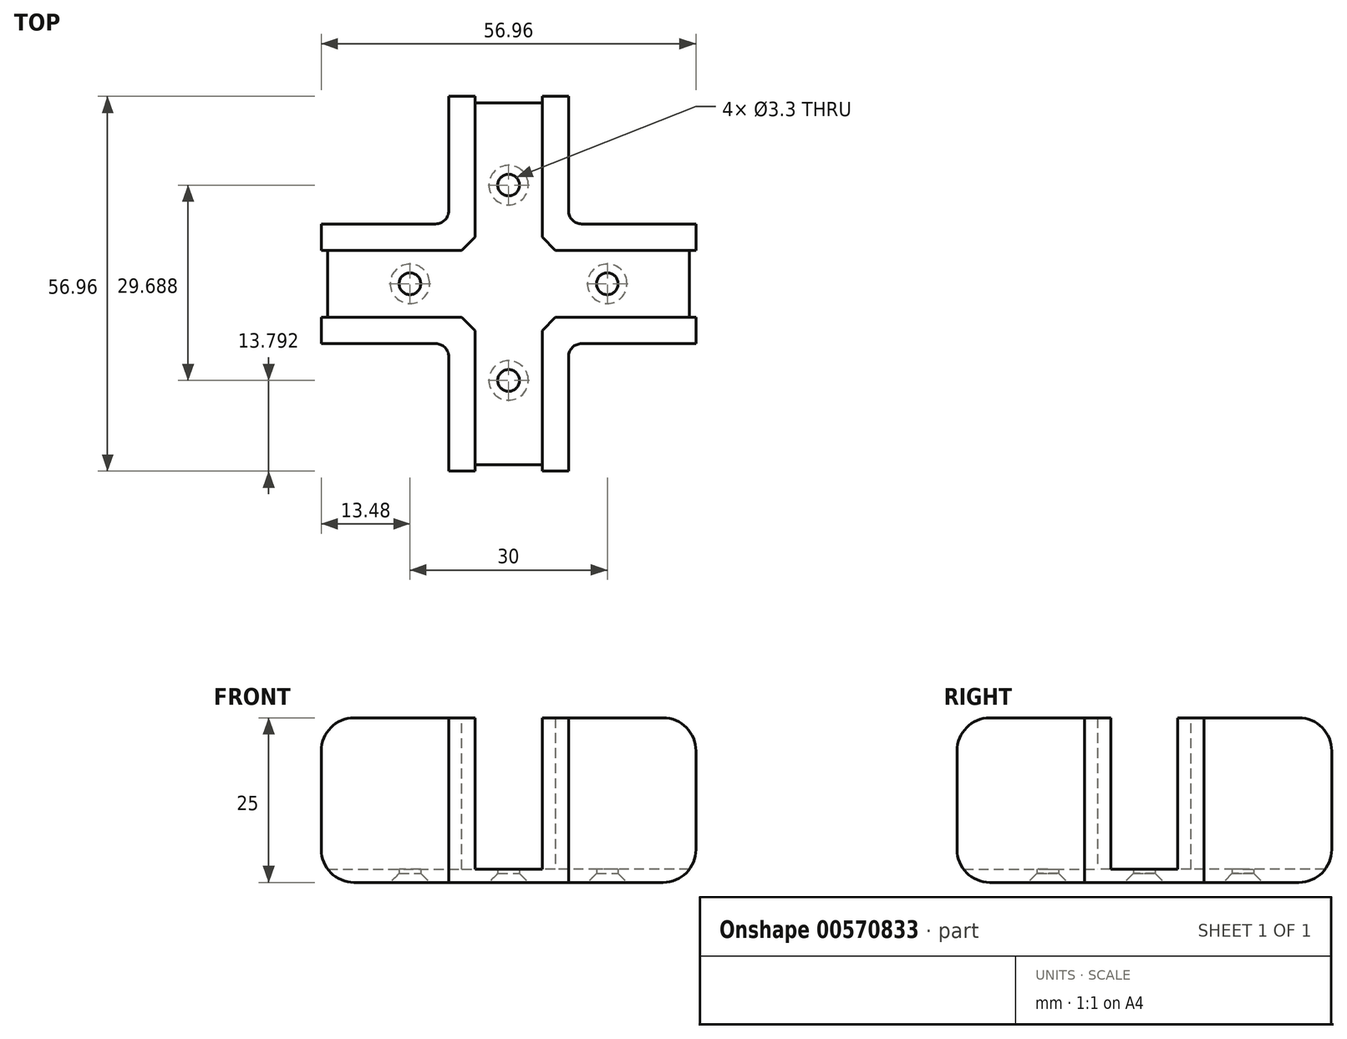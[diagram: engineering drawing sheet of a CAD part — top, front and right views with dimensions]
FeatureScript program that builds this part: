
annotation { "Feature Type Name" : "Feature", "Feature Type Description" : "" }
export const myFeature = defineFeature(function(context is Context, id is Id, definition is map)
    precondition{}
    {
        {
            var Q0;
            Q0=qCreatedBy(makeId("Top.planeOp"),FACE);
            var sketch = newSketch(context, id + "F0", { "sketchPlane" : qUnion([Q0])});
            skLineSegment(sketch, "E0", {"start": v(28.48, 10.2) * mm, "end": v(5.1, 10.2) * mm});
            skLineSegment(sketch, "E1", {"start": v(5.1, 10.2) * mm, "end": v(5.1, 33.58) * mm});
            skLineSegment(sketch, "E2", {"start": v(-5.1, 33.58) * mm, "end": v(-5.1, 10.2) * mm});
            skLineSegment(sketch, "E3", {"start": v(-5.1, 10.2) * mm, "end": v(-28.48, 10.2) * mm});
            skLineSegment(sketch, "E4.0", {"start": v(9.1, 33.58) * mm, "end": v(-9.1, 33.58) * mm});
            skLineSegment(sketch, "E4.1", {"start": v(9.1, 14.2) * mm, "end": v(9.1, 33.58) * mm});
            skLineSegment(sketch, "E4.2", {"start": v(-9.1, 33.58) * mm, "end": v(-9.1, 14.2) * mm});
            skLineSegment(sketch, "E4.3", {"start": v(28.48, 14.2) * mm, "end": v(9.1, 14.2) * mm});
            skLineSegment(sketch, "E4.4", {"start": v(28.48, -4) * mm, "end": v(28.48, 14.2) * mm});
            skLineSegment(sketch, "E4.5", {"start": v(-9.1, 14.2) * mm, "end": v(-28.48, 14.2) * mm});
            skLineSegment(sketch, "E4.6", {"start": v(-28.48, 14.2) * mm, "end": v(-28.48, -4) * mm});
            skLineSegment(sketch, "E5", {"start": v(-28.48, 0) * mm, "end": v(-5.1, 0) * mm});
            skLineSegment(sketch, "E6", {"start": v(-5.1, 0) * mm, "end": v(-5.1, -23.38) * mm});
            skLineSegment(sketch, "E7", {"start": v(5.1, -23.38) * mm, "end": v(5.1, 0) * mm});
            skLineSegment(sketch, "E8", {"start": v(5.1, 0) * mm, "end": v(28.48, 0) * mm});
            skLineSegment(sketch, "E9.0", {"start": v(9.1, -4) * mm, "end": v(28.48, -4) * mm});
            skLineSegment(sketch, "E9.1", {"start": v(-28.48, -4) * mm, "end": v(-9.1, -4) * mm});
            skLineSegment(sketch, "E9.2", {"start": v(-9.1, -4) * mm, "end": v(-9.1, -23.38) * mm});
            skLineSegment(sketch, "E9.3", {"start": v(-9.1, -23.38) * mm, "end": v(9.1, -23.38) * mm});
            skLineSegment(sketch, "E9.4", {"start": v(9.1, -23.38) * mm, "end": v(9.1, -4) * mm});
            skPoint(sketch, "E10", {"position": v(0, 33.58) * mm});
            skSolve(sketch);
        }
        {
            var Q0;
            Q0=qSketchRegion(id+"F0",true);
            extrude(context, id + "F1", {"entities" : qUnion([Q0]), "depth" : 2 * mm, "offsetDistance" : 25 * mm});
        }
        {
            var Q0;
            {var subQ1=sQuery(id+"F0.wireOp",EDGE,"E2");Q0=makeQuery(id+"F0.imprint","IMPRINT",FACE,{"disambiguationData":[TD([[makeQuery(id+"F0.imprint","IMPRINT",EDGE,{"derivedFrom":subQ1}),-1.0]])]});}
            var Q1;
            {var subQ4=sQuery(id+"F0.wireOp",EDGE,"E0");Q1=makeQuery(id+"F0.imprint","IMPRINT",FACE,{"disambiguationData":[TD([[makeQuery(id+"F0.imprint","IMPRINT",EDGE,{"derivedFrom":subQ4}),-1.0]])]});}
            var Q2;
            {var subQ2=sQuery(id+"F0.wireOp",EDGE,"E5");Q2=makeQuery(id+"F0.imprint","IMPRINT",FACE,{"disambiguationData":[TD([[makeQuery(id+"F0.imprint","IMPRINT",EDGE,{"derivedFrom":subQ2}),-1.0]])]});}
            var Q3;
            {var subQ3=sQuery(id+"F0.wireOp",EDGE,"E7");Q3=makeQuery(id+"F0.imprint","IMPRINT",FACE,{"disambiguationData":[TD([[makeQuery(id+"F0.imprint","IMPRINT",EDGE,{"derivedFrom":subQ3}),-1.0]])]});}
            extrude(context, id + "F2", {"entities" : qUnion([Q0, Q1, Q2, Q3]), "operationType" : NewBodyOperationType.ADD, "depth" : 25 * mm, "offsetDistance" : 25 * mm});
        }
        {
            var Q0;
            {var subQ0=sQuery(id+"F0.wireOp",EDGE,"E4.3");var subQ1=sQuery(id+"F0.wireOp",EDGE,"E4.1");Q0=makeQuery(id+"F2.boolean.opBoolean","MERGE",EDGE,{"derivedFrom":[makeQuery(id+"F1.opExtrude","SWEPT_EDGE",EDGE,{"disambiguationData":[OSD([subQ1,subQ0])]}),makeQuery(id+"F2.opExtrude","SWEPT_EDGE",EDGE,{"disambiguationData":[OSD([subQ1,subQ0])]})]});}
            var Q1;
            {var subQ0=sQuery(id+"F0.wireOp",EDGE,"E9.4");var subQ1=sQuery(id+"F0.wireOp",EDGE,"E9.0");Q1=makeQuery(id+"F2.boolean.opBoolean","MERGE",EDGE,{"derivedFrom":[makeQuery(id+"F1.opExtrude","SWEPT_EDGE",EDGE,{"disambiguationData":[OSD([subQ1,subQ0])]}),makeQuery(id+"F2.opExtrude","SWEPT_EDGE",EDGE,{"disambiguationData":[OSD([subQ1,subQ0])]})]});}
            fillet(context, id + "F3", {"entities" : qUnion([Q0, Q1]), "radius" : 2 * mm, "tangentPropagation" : true, "allowEdgeOverflow" : false});
        }
        {
            var Q0;
            {var subQ0=sQuery(id+"F0.wireOp",EDGE,"E4.4");Q0=makeQuery(id+"F2.opExtrude","CAP_EDGE",EDGE,{"disambiguationData":[OSD([subQ0]),TDD([makeQuery(id+"F0.imprint","IMPRINT",EDGE,{"disambiguationData":[TD([[makeQuery(id+"F0.imprint","INTERSECT",VERTEX,{"derivedFrom":[sQuery(id+"F0.wireOp",EDGE,"4AKFVKuP-VGzW-Z0gR-biP7-avwRZvC0l9sY"),subQ0]}),1.0]])],"derivedFrom":subQ0})])],"isStart":false});}
            var Q1;
            {var subQ0=sQuery(id+"F0.wireOp",EDGE,"E4.4");Q1=makeQuery(id+"F2.opExtrude","CAP_EDGE",EDGE,{"disambiguationData":[OSD([subQ0]),TDD([makeQuery(id+"F0.imprint","IMPRINT",EDGE,{"disambiguationData":[TD([[makeQuery(id+"F0.imprint","INTERSECT",VERTEX,{"derivedFrom":[sQuery(id+"F0.wireOp",EDGE,"E0"),subQ0]}),-1.0]])],"derivedFrom":subQ0})])],"isStart":false});}
            var Q2;
            {var subQ0=sQuery(id+"F0.wireOp",EDGE,"E4.6");Q2=makeQuery(id+"F2.opExtrude","CAP_EDGE",EDGE,{"disambiguationData":[OSD([subQ0]),TDD([makeQuery(id+"F0.imprint","IMPRINT",EDGE,{"disambiguationData":[TD([[makeQuery(id+"F0.imprint","INTERSECT",VERTEX,{"derivedFrom":[sQuery(id+"F0.wireOp",EDGE,"34O9V31c-Diq1-Ufnw-3ykA-mJ2vG209VLsY"),subQ0]}),-1.0]])],"derivedFrom":subQ0})])],"isStart":false});}
            var Q3;
            {var subQ0=sQuery(id+"F0.wireOp",EDGE,"E4.6");Q3=makeQuery(id+"F2.opExtrude","CAP_EDGE",EDGE,{"disambiguationData":[OSD([subQ0]),TDD([makeQuery(id+"F0.imprint","IMPRINT",EDGE,{"disambiguationData":[TD([[makeQuery(id+"F0.imprint","INTERSECT",VERTEX,{"derivedFrom":[sQuery(id+"F0.wireOp",EDGE,"E3"),subQ0]}),1.0]])],"derivedFrom":subQ0})])],"isStart":false});}
            var Q4;
            {var subQ0=sQuery(id+"F0.wireOp",EDGE,"E4.0");Q4=makeQuery(id+"F2.opExtrude","CAP_EDGE",EDGE,{"disambiguationData":[OSD([subQ0]),TDD([makeQuery(id+"F0.imprint","IMPRINT",EDGE,{"disambiguationData":[TD([[makeQuery(id+"F0.imprint","INTERSECT",VERTEX,{"derivedFrom":[sQuery(id+"F0.wireOp",EDGE,"E2"),subQ0]}),-1.0]])],"derivedFrom":subQ0})])],"isStart":false});}
            var Q5;
            {var subQ0=sQuery(id+"F0.wireOp",EDGE,"E4.0");Q5=makeQuery(id+"F2.opExtrude","CAP_EDGE",EDGE,{"disambiguationData":[OSD([subQ0]),TDD([makeQuery(id+"F0.imprint","IMPRINT",EDGE,{"disambiguationData":[TD([[makeQuery(id+"F0.imprint","INTERSECT",VERTEX,{"derivedFrom":[sQuery(id+"F0.wireOp",EDGE,"E1"),subQ0]}),1.0]])],"derivedFrom":subQ0})])],"isStart":false});}
            var Q6;
            Q6=makeQuery(id+"F1.opExtrude","CAP_EDGE",EDGE,{"disambiguationData":[OSD([sQuery(id+"F0.wireOp",EDGE,"E4.6")])],"isStart":true});
            var Q7;
            Q7=makeQuery(id+"F1.opExtrude","CAP_EDGE",EDGE,{"disambiguationData":[OSD([sQuery(id+"F0.wireOp",EDGE,"E4.4")])],"isStart":true});
            var Q8;
            Q8=makeQuery(id+"F1.opExtrude","CAP_EDGE",EDGE,{"disambiguationData":[OSD([sQuery(id+"F0.wireOp",EDGE,"E4.0")])],"isStart":true});
            var Q9;
            Q9=makeQuery(id+"F1.opExtrude","CAP_EDGE",EDGE,{"disambiguationData":[OSD([sQuery(id+"F0.wireOp",EDGE,"E9.3")])],"isStart":true});
            var Q10;
            {var subQ0=sQuery(id+"F0.wireOp",EDGE,"E9.3");Q10=makeQuery(id+"F2.opExtrude","CAP_EDGE",EDGE,{"disambiguationData":[OSD([subQ0]),TDD([makeQuery(id+"F0.imprint","IMPRINT",EDGE,{"disambiguationData":[TD([[makeQuery(id+"F0.imprint","INTERSECT",VERTEX,{"derivedFrom":[sQuery(id+"F0.wireOp",EDGE,"E6"),subQ0]}),1.0]])],"derivedFrom":subQ0})])],"isStart":false});}
            var Q11;
            {var subQ0=sQuery(id+"F0.wireOp",EDGE,"E9.3");Q11=makeQuery(id+"F2.opExtrude","CAP_EDGE",EDGE,{"disambiguationData":[OSD([subQ0]),TDD([makeQuery(id+"F0.imprint","IMPRINT",EDGE,{"disambiguationData":[TD([[makeQuery(id+"F0.imprint","INTERSECT",VERTEX,{"derivedFrom":[sQuery(id+"F0.wireOp",EDGE,"E7"),subQ0]}),-1.0]])],"derivedFrom":subQ0})])],"isStart":false});}
            fillet(context, id + "F4", {"entities" : qUnion([Q0, Q1, Q2, Q3, Q4, Q5, Q6, Q7, Q8, Q9, Q10, Q11]), "radius" : 5 * mm, "tangentPropagation" : true, "allowEdgeOverflow" : false});
        }
        {
            var Q0;
            {var subQ0=sQuery(id+"F0.wireOp",EDGE,"E4.5");var subQ1=sQuery(id+"F0.wireOp",EDGE,"E4.2");Q0=makeQuery(id+"F2.boolean.opBoolean","MERGE",EDGE,{"derivedFrom":[makeQuery(id+"F1.opExtrude","SWEPT_EDGE",EDGE,{"disambiguationData":[OSD([subQ1,subQ0])]}),makeQuery(id+"F2.opExtrude","SWEPT_EDGE",EDGE,{"disambiguationData":[OSD([subQ1,subQ0])]})]});}
            var Q1;
            {var subQ0=sQuery(id+"F0.wireOp",EDGE,"E9.2");var subQ1=sQuery(id+"F0.wireOp",EDGE,"E9.1");Q1=makeQuery(id+"F2.boolean.opBoolean","MERGE",EDGE,{"derivedFrom":[makeQuery(id+"F1.opExtrude","SWEPT_EDGE",EDGE,{"disambiguationData":[OSD([subQ1,subQ0])]}),makeQuery(id+"F2.opExtrude","SWEPT_EDGE",EDGE,{"disambiguationData":[OSD([subQ1,subQ0])]})]});}
            fillet(context, id + "F5", {"entities" : qUnion([Q0, Q1]), "radius" : 2 * mm, "tangentPropagation" : true, "allowEdgeOverflow" : false});
        }
        {
            var Q0;
            Q0=makeQuery(id+"F2.opExtrude","SWEPT_EDGE",EDGE,{"disambiguationData":[OSD([sQuery(id+"F0.wireOp",EDGE,"E0"),sQuery(id+"F0.wireOp",EDGE,"E1")])]});
            var Q1;
            Q1=makeQuery(id+"F2.opExtrude","SWEPT_EDGE",EDGE,{"disambiguationData":[OSD([sQuery(id+"F0.wireOp",EDGE,"E2"),sQuery(id+"F0.wireOp",EDGE,"E3")])]});
            var Q2;
            Q2=makeQuery(id+"F2.opExtrude","SWEPT_EDGE",EDGE,{"disambiguationData":[OSD([sQuery(id+"F0.wireOp",EDGE,"E7"),sQuery(id+"F0.wireOp",EDGE,"E8")])]});
            var Q3;
            Q3=makeQuery(id+"F2.opExtrude","SWEPT_EDGE",EDGE,{"disambiguationData":[OSD([sQuery(id+"F0.wireOp",EDGE,"E5"),sQuery(id+"F0.wireOp",EDGE,"E6")])]});
            chamfer(context, id + "F6", {"entities" : qUnion([Q0, Q1, Q2, Q3]), "width" : 2 * mm, "tangentPropagation" : true});
        }
        {
            var Q0;
            {var subQ9=sQuery(id+"F0.wireOp",EDGE,"E0");Q0=makeQuery(id+"F0.imprint","IMPRINT",FACE,{"disambiguationData":[TD([[makeQuery(id+"F0.imprint","IMPRINT",EDGE,{"derivedFrom":subQ9}),1.0]])]});}
            var sketch = newSketch(context, id + "F7", { "sketchPlane" : qUnion([Q0])});
            skLineSegment(sketch, "E11", {"start": v(0, -18.75) * mm, "end": v(0, 32.62) * mm});
            skLineSegment(sketch, "E12", {"start": v(-27.5, 5.1) * mm, "end": v(28.43, 5.1) * mm});
            skPoint(sketch, "E13", {"position": v(-15, 5.1) * mm});
            skPoint(sketch, "E14", {"position": v(15, 5.1) * mm});
            skPoint(sketch, "E15", {"position": v(0, -9.59) * mm});
            skPoint(sketch, "E16", {"position": v(0, 20.1) * mm});
            skSolve(sketch);
        }
        {
            var Q0;
            Q0=sQuery(id+"F7.wireOp",VERTEX,"E15");
            var Q1;
            Q1=sQuery(id+"F7.wireOp",VERTEX,"E13");
            var Q2;
            Q2=sQuery(id+"F7.wireOp",VERTEX,"E14");
            var Q3;
            Q3=sQuery(id+"F7.wireOp",VERTEX,"E16");
            var Q4;
            Q4=makeQuery(id+"F1.opExtrude","SWEPT_BODY",BODY,{"disambiguationData":[OSD([sQuery(id+"F0.wireOp",EDGE,"E4.0"),sQuery(id+"F0.wireOp",EDGE,"E4.1"),sQuery(id+"F0.wireOp",EDGE,"E4.2"),sQuery(id+"F0.wireOp",EDGE,"E4.3"),sQuery(id+"F0.wireOp",EDGE,"E4.4"),sQuery(id+"F0.wireOp",EDGE,"E4.5"),sQuery(id+"F0.wireOp",EDGE,"E4.6"),sQuery(id+"F0.wireOp",EDGE,"E9.0"),sQuery(id+"F0.wireOp",EDGE,"E9.1"),sQuery(id+"F0.wireOp",EDGE,"E9.2"),sQuery(id+"F0.wireOp",EDGE,"E9.3"),sQuery(id+"F0.wireOp",EDGE,"E9.4")])]});
            hole(context, id + "F8", {"style" : HoleStyle.C_SINK, "endStyle" : HoleEndStyle.THROUGH, "oppositeDirection" : true, "holeDiameter" : 3.3 * mm, "cSinkDiameter" : 6 * mm, "cSinkAngle" : 90 * degree, "majorDiameter" : 3 * mm, "isTappedThrough" : true, "tappedDepth" : 12 * mm, "tapClearance" : 3, "locations" : qUnion([Q0, Q1, Q2, Q3]), "scope" : qUnion([Q4])});
        }
    });
